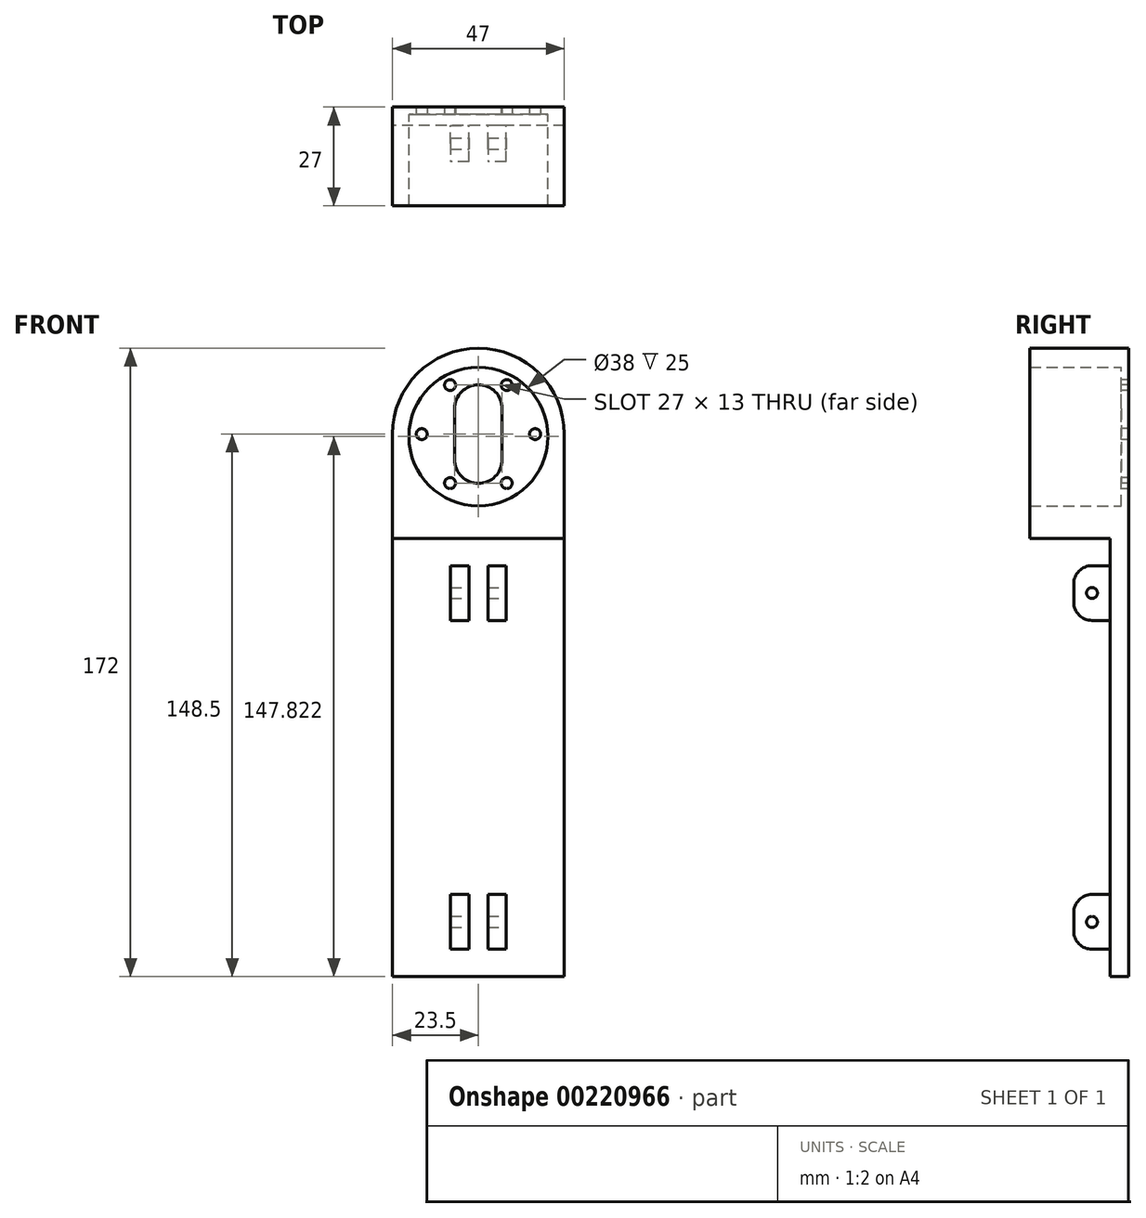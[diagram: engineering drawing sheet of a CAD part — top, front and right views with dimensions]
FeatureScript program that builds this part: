
annotation { "Feature Type Name" : "Feature", "Feature Type Description" : "" }
export const myFeature = defineFeature(function(context is Context, id is Id, definition is map)
    precondition{}
    {
        {
            var Q0;
            Q0=qCreatedBy(makeId("Front.planeOp"),FACE);
            var sketch = newSketch(context, id + "F0", { "sketchPlane" : qUnion([Q0])});
            skLineSegment(sketch, "E0", {"start": v(0, -23.5) * mm, "end": v(-23.5, -23.5) * mm});
            skLineSegment(sketch, "E1", {"start": v(-23.5, -23.5) * mm, "end": v(-23.5, 0) * mm});
            skLineSegment(sketch, "E2", {"start": v(0, -23.5) * mm, "end": v(23.5, -23.5) * mm});
            skLineSegment(sketch, "E3", {"start": v(23.5, -23.5) * mm, "end": v(23.5, 0) * mm});
            skArc(sketch, "E4", {"start": v(-23.5, 0) * mm, "mid": v(0, 23.5) * mm, "end": v(23.5, 0) * mm});
            skSolve(sketch);
        }
        {
            var Q0;
            Q0=qSketchRegion(id+"F0",true);
            extrude(context, id + "F1", {"entities" : qUnion([Q0]), "depth" : 2 * mm});
        }
        {
            var Q0;
            Q0=makeQuery(id+"F1.opExtrude","CAP_FACE",FACE,{"disambiguationData":[OSD([sQuery(id+"F0.wireOp",EDGE,"E0"),sQuery(id+"F0.wireOp",EDGE,"E1"),sQuery(id+"F0.wireOp",EDGE,"E2"),sQuery(id+"F0.wireOp",EDGE,"E3"),sQuery(id+"F0.wireOp",EDGE,"E4")])],"isStart":false});
            var sketch = newSketch(context, id + "F2", { "sketchPlane" : qUnion([Q0])});
            skCircle(sketch, "E5", {"center": v(15.5, 0) * mm, "radius": 1.5 * mm});
            skCircle(sketch, "E6.1.0", {"center": v(7.75, 13.42) * mm, "radius": 1.5 * mm});
            skCircle(sketch, "E6.2.0", {"center": v(-7.75, 13.42) * mm, "radius": 1.5 * mm});
            skCircle(sketch, "E6.3.0", {"center": v(-15.5, 0) * mm, "radius": 1.5 * mm});
            skCircle(sketch, "E6.4.0", {"center": v(-7.75, -13.42) * mm, "radius": 1.5 * mm});
            skCircle(sketch, "E6.5.0", {"center": v(7.75, -13.42) * mm, "radius": 1.5 * mm});
            skPoint(sketch, "E6.center", {"position": v(0, 0) * mm});
            skLineSegment(sketch, "E7", {"start": v(6.5, 7) * mm, "end": v(6.5, -7) * mm});
            skLineSegment(sketch, "E8", {"start": v(-6.5, -7) * mm, "end": v(-6.5, 7) * mm});
            skArc(sketch, "E9", {"start": v(-6.5, 7) * mm, "mid": v(0, 13.5) * mm, "end": v(6.5, 7) * mm});
            skArc(sketch, "E10", {"start": v(-6.5, -7) * mm, "mid": v(0, -13.5) * mm, "end": v(6.5, -7) * mm});
            skSolve(sketch);
        }
        {
            var Q0;
            Q0=qSketchRegion(id+"F2",true);
            extrude(context, id + "F3", {"entities" : qUnion([Q0]), "operationType" : NewBodyOperationType.REMOVE, "oppositeDirection" : true, "depth" : 5 * mm});
        }
        {
            var Q0;
            Q0=qCreatedBy(makeId("Front.planeOp"),FACE);
            var sketch = newSketch(context, id + "F4", { "sketchPlane" : qUnion([Q0])});
            skCircle(sketch, "E11", {"center": v(0, -0.68) * mm, "radius": 19 * mm});
            skLineSegment(sketch, "E12", {"start": v(-23.5, 0) * mm, "end": v(-23.5, -23.5) * mm});
            skLineSegment(sketch, "E13", {"start": v(-23.5, -23.5) * mm, "end": v(23.5, -23.5) * mm});
            skLineSegment(sketch, "E14", {"start": v(23.5, -23.5) * mm, "end": v(23.5, 0) * mm});
            skArc(sketch, "E15", {"start": v(-23.5, 0) * mm, "mid": v(0, 23.5) * mm, "end": v(23.5, 0) * mm});
            skSolve(sketch);
        }
        {
            var Q0;
            Q0=qSketchRegion(id+"F4",true);
            extrude(context, id + "F5", {"entities" : qUnion([Q0]), "operationType" : NewBodyOperationType.ADD, "offsetDistance" : 25 * mm, "depth" : 27 * mm});
        }
        {
            var Q0;
            Q0=makeQuery(id+"F5.boolean.opBoolean","MERGE",FACE,{"derivedFrom":[makeQuery(id+"F1.opExtrude","SWEPT_FACE",FACE,{"disambiguationData":[OSD([sQuery(id+"F0.wireOp",EDGE,"E0"),sQuery(id+"F0.wireOp",EDGE,"E2")])]}),makeQuery(id+"F5.opExtrude","SWEPT_FACE",FACE,{"disambiguationData":[OSD([sQuery(id+"F4.wireOp",EDGE,"E13")])]})]});
            var sketch = newSketch(context, id + "F6", { "sketchPlane" : qUnion([Q0])});
            skLineSegment(sketch, "E16.bottom", {"start": v(-23.5, 27) * mm, "end": v(23.5, 27) * mm});
            skLineSegment(sketch, "E16.top", {"start": v(-23.5, 0) * mm, "end": v(23.5, 0) * mm});
            skLineSegment(sketch, "E16.left", {"start": v(-23.5, 27) * mm, "end": v(-23.5, 0) * mm});
            skLineSegment(sketch, "E16.right", {"start": v(23.5, 27) * mm, "end": v(23.5, 0) * mm});
            skSolve(sketch);
        }
        {
            var Q0;
            Q0=qSketchRegion(id+"F6",true);
            extrude(context, id + "F7", {"entities" : qUnion([Q0]), "operationType" : NewBodyOperationType.ADD, "depth" : 5 * mm});
        }
        {
            var Q0;
            Q0=makeQuery(id+"F7.opExtrude","CAP_FACE",FACE,{"disambiguationData":[OSD([sQuery(id+"F6.wireOp",EDGE,"E16.bottom"),sQuery(id+"F6.wireOp",EDGE,"E16.top"),sQuery(id+"F6.wireOp",EDGE,"E16.left"),sQuery(id+"F6.wireOp",EDGE,"E16.right")])],"isStart":false});
            var sketch = newSketch(context, id + "F8", { "sketchPlane" : qUnion([Q0])});
            skLineSegment(sketch, "E17", {"start": v(-23.5, 0) * mm, "end": v(23.5, 0) * mm});
            skLineSegment(sketch, "E18", {"start": v(23.5, 0) * mm, "end": v(23.5, 5) * mm});
            skLineSegment(sketch, "E19", {"start": v(23.5, 5) * mm, "end": v(-23.5, 5) * mm});
            skLineSegment(sketch, "E20", {"start": v(-23.5, 5) * mm, "end": v(-23.5, 0) * mm});
            skSolve(sketch);
        }
        {
            var Q0;
            Q0 = qSketchRegion(id + "F8", true);
            extrude(context, id + "F9", {"entities" : qUnion([Q0]), "operationType" : NewBodyOperationType.ADD, "depth" : 120 * mm, "offsetDistance" : 25 * mm});
        }
        {
            var Q0;
            Q0=makeQuery(id+"F9.opExtrude","SWEPT_FACE",FACE,{"disambiguationData":[OSD([sQuery(id+"F8.wireOp",EDGE,"E19")])]});
            var sketch = newSketch(context, id + "F10", { "sketchPlane" : qUnion([Q0])});
            skLineSegment(sketch, "E21", {"start": v(0, -28.5) * mm, "end": v(0, -148.5) * mm});
            skLineSegment(sketch, "E22", {"start": v(0, -88.5) * mm, "end": v(0, -133.5) * mm});
            skLineSegment(sketch, "E23", {"start": v(0, -133.5) * mm, "end": v(0, -88.5) * mm});
            skLineSegment(sketch, "E24", {"start": v(0, -88.5) * mm, "end": v(0, -43.5) * mm});
            skLineSegment(sketch, "E25", {"start": v(0, -43.5) * mm, "end": v(-2.6, -43.5) * mm});
            skLineSegment(sketch, "E26", {"start": v(-2.6, -43.5) * mm, "end": v(-2.6, -36) * mm});
            skLineSegment(sketch, "E27", {"start": v(-2.6, -43.5) * mm, "end": v(-2.6, -51) * mm});
            skLineSegment(sketch, "E28", {"start": v(-2.6, -51) * mm, "end": v(-7.6, -51) * mm});
            skLineSegment(sketch, "E29", {"start": v(-7.6, -51) * mm, "end": v(-7.6, -36) * mm});
            skLineSegment(sketch, "E30", {"start": v(-7.6, -36) * mm, "end": v(-2.6, -36) * mm});
            skLineSegment(sketch, "E31", {"start": v(0, -133.5) * mm, "end": v(2.6, -133.5) * mm});
            skLineSegment(sketch, "E32", {"start": v(2.6, -133.5) * mm, "end": v(2.6, -141) * mm});
            skLineSegment(sketch, "E33", {"start": v(2.6, -141) * mm, "end": v(7.6, -141) * mm});
            skLineSegment(sketch, "E34", {"start": v(7.6, -141) * mm, "end": v(7.6, -126) * mm});
            skLineSegment(sketch, "E35", {"start": v(7.6, -126) * mm, "end": v(2.6, -126) * mm});
            skLineSegment(sketch, "E36", {"start": v(2.6, -126) * mm, "end": v(2.6, -133.5) * mm});
            skLineSegment(sketch, "E37", {"start": v(0, -43.5) * mm, "end": v(2.6, -43.5) * mm});
            skLineSegment(sketch, "E38", {"start": v(2.6, -43.5) * mm, "end": v(2.6, -36) * mm});
            skLineSegment(sketch, "E39", {"start": v(2.6, -36) * mm, "end": v(7.6, -36) * mm});
            skLineSegment(sketch, "E40", {"start": v(7.6, -36) * mm, "end": v(7.6, -51) * mm});
            skLineSegment(sketch, "E41", {"start": v(7.6, -51) * mm, "end": v(2.6, -51) * mm});
            skLineSegment(sketch, "E42", {"start": v(2.6, -51) * mm, "end": v(2.6, -43.5) * mm});
            skLineSegment(sketch, "E43", {"start": v(0, -133.5) * mm, "end": v(-2.6, -133.5) * mm});
            skLineSegment(sketch, "E44", {"start": v(-2.6, -133.5) * mm, "end": v(-2.6, -126) * mm});
            skLineSegment(sketch, "E45", {"start": v(-2.6, -126) * mm, "end": v(-7.6, -126) * mm});
            skLineSegment(sketch, "E46", {"start": v(-7.6, -126) * mm, "end": v(-7.6, -141) * mm});
            skLineSegment(sketch, "E47", {"start": v(-7.6, -141) * mm, "end": v(-2.6, -141) * mm});
            skLineSegment(sketch, "E48", {"start": v(-2.6, -141) * mm, "end": v(-2.6, -133.5) * mm});
            skSolve(sketch);
        }
        {
            var Q0;
            {Q0=qUnion([makeQuery(id+"F10.imprint","IMPRINT",FACE,{"disambiguationData":[TD([[makeQuery(id+"F10.imprint","IMPRINT",EDGE,{"derivedFrom":sQuery(id+"F10.wireOp",EDGE,"E26")}),1.0]])]}),makeQuery(id+"F10.imprint","IMPRINT",FACE,{"disambiguationData":[TD([[makeQuery(id+"F10.imprint","IMPRINT",EDGE,{"derivedFrom":sQuery(id+"F10.wireOp",EDGE,"E32")}),1.0]])]}),makeQuery(id+"F10.imprint","IMPRINT",FACE,{"disambiguationData":[TD([[makeQuery(id+"F10.imprint","IMPRINT",EDGE,{"derivedFrom":sQuery(id+"F10.wireOp",EDGE,"E38")}),-1.0]])]}),makeQuery(id+"F10.imprint","IMPRINT",FACE,{"disambiguationData":[TD([[makeQuery(id+"F10.imprint","IMPRINT",EDGE,{"derivedFrom":sQuery(id+"F10.wireOp",EDGE,"E44")}),1.0]])]})]);}
            extrude(context, id + "F11", {"entities" : qUnion([Q0]), "operationType" : NewBodyOperationType.ADD, "depth" : 10 * mm, "offsetDistance" : 25 * mm});
        }
        {
            var Q0;
            Q0=makeQuery(id+"F11.opExtrude","SWEPT_FACE",FACE,{"disambiguationData":[OSD([sQuery(id+"F10.wireOp",EDGE,"E40")])]});
            var sketch = newSketch(context, id + "F12", { "sketchPlane" : qUnion([Q0])});
            skLineSegment(sketch, "E49", {"start": v(-15, -36) * mm, "end": v(-5, -51) * mm});
            skLineSegment(sketch, "E50", {"start": v(-15, -51) * mm, "end": v(-5, -36) * mm});
            skCircle(sketch, "E51", {"center": v(-10, -43.5) * mm, "radius": 1.5 * mm});
            skSolve(sketch);
        }
        {
            var Q0;
            Q0 = qSketchRegion(id + "F12", true);
            extrude(context, id + "F13", {"entities" : qUnion([Q0]), "operationType" : NewBodyOperationType.REMOVE, "oppositeDirection" : true, "depth" : 25 * mm, "offsetDistance" : 25 * mm});
        }
        {
            var Q0;
            Q0=makeQuery(id+"F11.opExtrude","SWEPT_FACE",FACE,{"disambiguationData":[OSD([sQuery(id+"F10.wireOp",EDGE,"E34")])]});
            var sketch = newSketch(context, id + "F14", { "sketchPlane" : qUnion([Q0])});
            skLineSegment(sketch, "E52", {"start": v(-15, -126) * mm, "end": v(-5, -141) * mm});
            skLineSegment(sketch, "E53", {"start": v(-15, -141) * mm, "end": v(-5, -126) * mm});
            skCircle(sketch, "E54", {"center": v(-10, -133.5) * mm, "radius": 1.5 * mm});
            skSolve(sketch);
        }
        {
            var Q0;
            Q0 = qSketchRegion(id + "F14", true);
            extrude(context, id + "F15", {"entities" : qUnion([Q0]), "operationType" : NewBodyOperationType.REMOVE, "oppositeDirection" : true, "depth" : 25 * mm, "offsetDistance" : 25 * mm});
        }
        {
            var Q0;
            Q0=makeQuery(id+"F11.opExtrude","CAP_EDGE",EDGE,{"disambiguationData":[OSD([sQuery(id+"F10.wireOp",EDGE,"E33")])],"isStart":false});
            var Q1;
            Q1=makeQuery(id+"F11.opExtrude","CAP_EDGE",EDGE,{"disambiguationData":[OSD([sQuery(id+"F10.wireOp",EDGE,"E35")])],"isStart":false});
            var Q2;
            Q2=makeQuery(id+"F11.opExtrude","CAP_EDGE",EDGE,{"disambiguationData":[OSD([sQuery(id+"F10.wireOp",EDGE,"E45")])],"isStart":false});
            var Q3;
            Q3=makeQuery(id+"F11.opExtrude","CAP_EDGE",EDGE,{"disambiguationData":[OSD([sQuery(id+"F10.wireOp",EDGE,"E47")])],"isStart":false});
            var Q4;
            Q4=makeQuery(id+"F11.opExtrude","CAP_EDGE",EDGE,{"disambiguationData":[OSD([sQuery(id+"F10.wireOp",EDGE,"E41")])],"isStart":false});
            var Q5;
            Q5=makeQuery(id+"F11.opExtrude","CAP_EDGE",EDGE,{"disambiguationData":[OSD([sQuery(id+"F10.wireOp",EDGE,"E39")])],"isStart":false});
            var Q6;
            Q6=makeQuery(id+"F11.opExtrude","CAP_EDGE",EDGE,{"disambiguationData":[OSD([sQuery(id+"F10.wireOp",EDGE,"E30")])],"isStart":false});
            var Q7;
            Q7=makeQuery(id+"F11.opExtrude","CAP_EDGE",EDGE,{"disambiguationData":[OSD([sQuery(id+"F10.wireOp",EDGE,"E28")])],"isStart":false});
            fillet(context, id + "F16", {"entities" : qUnion([Q0, Q1, Q2, Q3, Q4, Q5, Q6, Q7]), "radius" : 5 * mm, "tangentPropagation" : true, "allowEdgeOverflow" : false});
        }
    });
